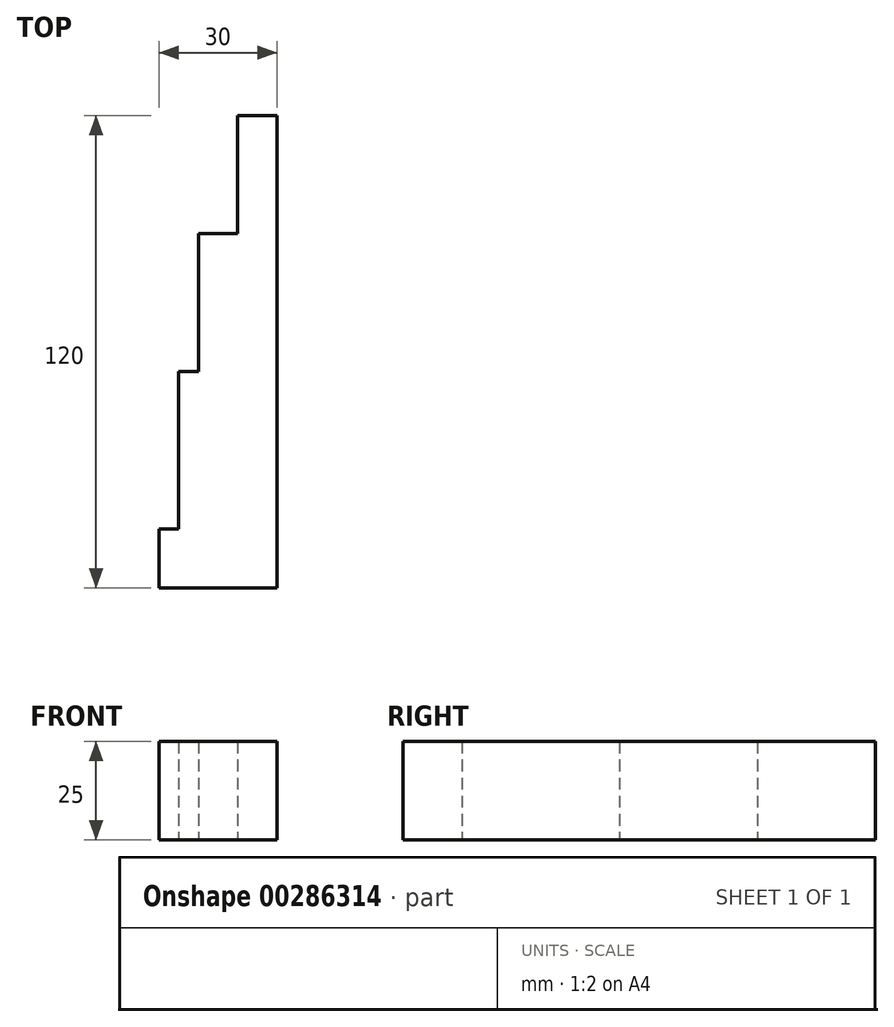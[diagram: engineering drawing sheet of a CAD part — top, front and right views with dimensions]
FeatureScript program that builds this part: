
annotation { "Feature Type Name" : "Feature", "Feature Type Description" : "" }
export const myFeature = defineFeature(function(context is Context, id is Id, definition is map)
    precondition{}
    {
        {
            var Q0;
            Q0=qCreatedBy(makeId("Top.planeOp"),FACE);
            var sketch = newSketch(context, id + "F0", { "sketchPlane" : qUnion([Q0])});
            skLineSegment(sketch, "E0", {"start": v(-35.8, -60.48) * mm, "end": v(-5.8, -60.48) * mm});
            skLineSegment(sketch, "E1", {"start": v(-5.8, -60.48) * mm, "end": v(-5.8, 59.52) * mm});
            skLineSegment(sketch, "E2", {"start": v(-5.8, 59.52) * mm, "end": v(-15.8, 59.52) * mm});
            skLineSegment(sketch, "E3", {"start": v(-15.8, 59.52) * mm, "end": v(-15.8, 29.52) * mm});
            skLineSegment(sketch, "E4", {"start": v(-15.8, 29.52) * mm, "end": v(-25.8, 29.52) * mm});
            skLineSegment(sketch, "E5", {"start": v(-25.8, 29.52) * mm, "end": v(-25.8, -5.48) * mm});
            skLineSegment(sketch, "E6", {"start": v(-25.8, -5.48) * mm, "end": v(-30.8, -5.48) * mm});
            skLineSegment(sketch, "E7", {"start": v(-30.8, -5.48) * mm, "end": v(-30.8, -45.48) * mm});
            skLineSegment(sketch, "E8", {"start": v(-30.8, -45.48) * mm, "end": v(-35.8, -45.48) * mm});
            skLineSegment(sketch, "E9", {"start": v(-35.8, -45.48) * mm, "end": v(-35.8, -60.48) * mm});
            skSolve(sketch);
        }
        {
            var Q0;
            Q0=makeQuery(id+"F0.imprint","IMPRINT",FACE,{"disambiguationData":[TD([[makeQuery(id+"F0.imprint","IMPRINT",EDGE,{"derivedFrom":sQuery(id+"F0.wireOp",EDGE,"E0")}),1.0]])]});
            extrude(context, id + "F1", {"entities" : qUnion([Q0]), "depth" : 25 * mm});
        }
    });
